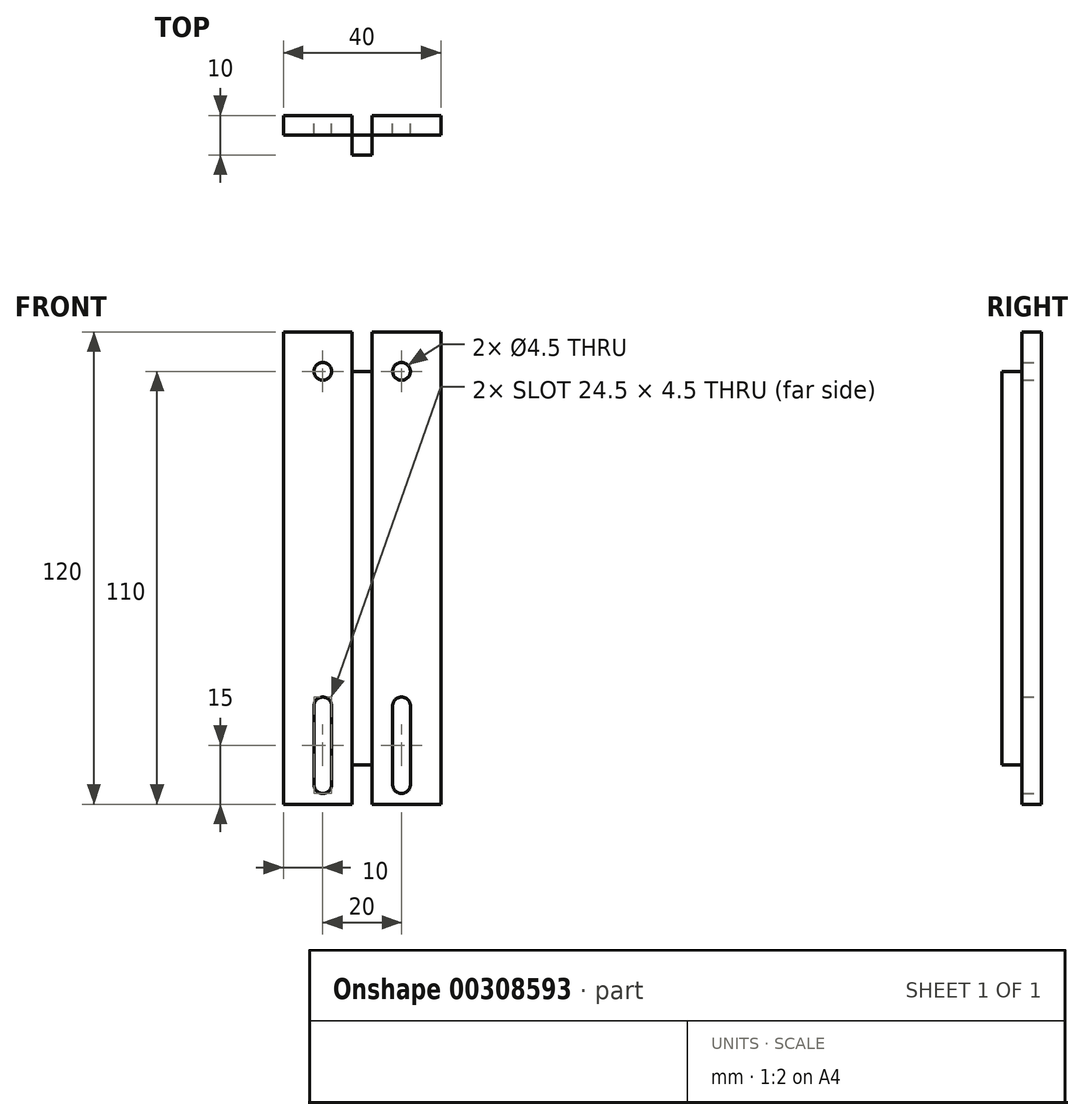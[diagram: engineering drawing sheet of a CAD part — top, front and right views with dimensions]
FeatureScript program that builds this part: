
annotation { "Feature Type Name" : "Feature", "Feature Type Description" : "" }
export const myFeature = defineFeature(function(context is Context, id is Id, definition is map)
    precondition{}
    {
        {
            var Q0;
            Q0=qCreatedBy(makeId("Front.planeOp"),FACE);
            var sketch = newSketch(context, id + "F0", { "sketchPlane" : qUnion([Q0])});
            skLineSegment(sketch, "E0.bottom", {"start": v(-20, 60) * mm, "end": v(20, 60) * mm});
            skLineSegment(sketch, "E0.top", {"start": v(-20, -60) * mm, "end": v(20, -60) * mm});
            skLineSegment(sketch, "E0.left", {"start": v(-20, 60) * mm, "end": v(-20, -60) * mm});
            skLineSegment(sketch, "E0.right", {"start": v(20, 60) * mm, "end": v(20, -60) * mm});
            skPoint(sketch, "E0.middle", {"position": v(0, 0) * mm});
            skPoint(sketch, "E1", {"position": v(-10, 50) * mm});
            skPoint(sketch, "E2", {"position": v(10, 50) * mm});
            skCircle(sketch, "E3", {"center": v(-10, -55) * mm, "radius": 2.25 * mm});
            skCircle(sketch, "E4", {"center": v(10, -55) * mm, "radius": 2.25 * mm});
            skCircle(sketch, "E5", {"center": v(-10, -35) * mm, "radius": 2.25 * mm});
            skCircle(sketch, "E6", {"center": v(10, -35) * mm, "radius": 2.25 * mm});
            skLineSegment(sketch, "E7", {"start": v(-20, -35) * mm, "end": v(20, -35) * mm, "construction": true});
            skLineSegment(sketch, "E8", {"start": v(-20, -55) * mm, "end": v(20, -55) * mm, "construction": true});
            skLineSegment(sketch, "E9", {"start": v(-12.25, -55) * mm, "end": v(-12.25, -35) * mm});
            skLineSegment(sketch, "E10", {"start": v(-7.75, -35) * mm, "end": v(-7.75, -55) * mm});
            skLineSegment(sketch, "E11", {"start": v(7.75, -35) * mm, "end": v(7.75, -55) * mm});
            skLineSegment(sketch, "E12", {"start": v(12.25, -35) * mm, "end": v(12.25, -55) * mm});
            skLineSegment(sketch, "E13.bottom", {"start": v(2.5, 60) * mm, "end": v(-2.5, 60) * mm});
            skLineSegment(sketch, "E13.top", {"start": v(2.5, -60) * mm, "end": v(-2.5, -60) * mm});
            skLineSegment(sketch, "E13.left", {"start": v(2.5, 60) * mm, "end": v(2.5, -60) * mm});
            skLineSegment(sketch, "E13.right", {"start": v(-2.5, 60) * mm, "end": v(-2.5, -60) * mm});
            skSolve(sketch);
        }
        {
            var Q0;
            {var subQ0=sQuery(id+"F0.wireOp",EDGE,"E0.left");Q0=makeQuery(id+"F0.imprint","IMPRINT",FACE,{"disambiguationData":[TD([[makeQuery(id+"F0.imprint","IMPRINT",EDGE,{"derivedFrom":subQ0}),1.0]])]});}
            var Q1;
            Q1=makeQuery(id+"F0.imprint","IMPRINT",FACE,{"disambiguationData":[TD([[makeQuery(id+"F0.imprint","IMPRINT",EDGE,{"derivedFrom":sQuery(id+"F0.wireOp",EDGE,"E13.bottom")}),1.0]])]});
            var Q2;
            {var subQ4=sQuery(id+"F0.wireOp",EDGE,"E0.right");Q2=makeQuery(id+"F0.imprint","IMPRINT",FACE,{"disambiguationData":[TD([[makeQuery(id+"F0.imprint","IMPRINT",EDGE,{"derivedFrom":subQ4}),-1.0]])]});}
            extrude(context, id + "F1", {"entities" : qUnion([Q0, Q1, Q2]), "depth" : 5 * mm});
        }
        {
            var Q0;
            Q0=makeQuery(id+"F1.opExtrude","CAP_FACE",FACE,{"disambiguationData":[OSD([sQuery(id+"F0.wireOp",EDGE,"E0.bottom"),sQuery(id+"F0.wireOp",EDGE,"E0.top"),sQuery(id+"F0.wireOp",EDGE,"E0.left"),sQuery(id+"F0.wireOp",EDGE,"E0.right"),sQuery(id+"F0.wireOp",EDGE,"E3"),sQuery(id+"F0.wireOp",EDGE,"E4"),sQuery(id+"F0.wireOp",EDGE,"E5"),sQuery(id+"F0.wireOp",EDGE,"E6"),sQuery(id+"F0.wireOp",EDGE,"E9"),sQuery(id+"F0.wireOp",EDGE,"E10"),sQuery(id+"F0.wireOp",EDGE,"E11"),sQuery(id+"F0.wireOp",EDGE,"E12"),sQuery(id+"F0.wireOp",EDGE,"E13.bottom"),sQuery(id+"F0.wireOp",EDGE,"E13.top")])],"isStart":false});
            var sketch = newSketch(context, id + "F2", { "sketchPlane" : qUnion([Q0])});
            skLineSegment(sketch, "E14.bottom", {"start": v(2.5, 50) * mm, "end": v(-2.5, 50) * mm});
            skLineSegment(sketch, "E14.top", {"start": v(2.5, -50) * mm, "end": v(-2.5, -50) * mm});
            skLineSegment(sketch, "E14.left", {"start": v(2.5, 50) * mm, "end": v(2.5, -50) * mm});
            skLineSegment(sketch, "E14.right", {"start": v(-2.5, 50) * mm, "end": v(-2.5, -50) * mm});
            skPoint(sketch, "E14.middle", {"position": v(0, 0) * mm});
            skSolve(sketch);
        }
        {
            var Q0;
            Q0=makeQuery(id+"F2.imprint","IMPRINT",FACE,{"disambiguationData":[TD([[makeQuery(id+"F2.imprint","IMPRINT",EDGE,{"derivedFrom":sQuery(id+"F2.wireOp",EDGE,"E14.bottom")}),1.0]])]});
            extrude(context, id + "F3", {"entities" : qUnion([Q0]), "operationType" : NewBodyOperationType.ADD, "depth" : 5 * mm});
        }
        {
            var Q0;
            Q0=sQuery(id+"F0.wireOp",VERTEX,"E2");
            var Q1;
            Q1=sQuery(id+"F0.wireOp",VERTEX,"E1");
            var Q2;
            Q2=makeQuery(id+"F1.opExtrude","SWEPT_BODY",BODY,{"disambiguationData":[OSD([sQuery(id+"F0.wireOp",EDGE,"E0.bottom"),sQuery(id+"F0.wireOp",EDGE,"E0.top"),sQuery(id+"F0.wireOp",EDGE,"E0.left"),sQuery(id+"F0.wireOp",EDGE,"E0.right"),sQuery(id+"F0.wireOp",EDGE,"E3"),sQuery(id+"F0.wireOp",EDGE,"E4"),sQuery(id+"F0.wireOp",EDGE,"E5"),sQuery(id+"F0.wireOp",EDGE,"E6"),sQuery(id+"F0.wireOp",EDGE,"E9"),sQuery(id+"F0.wireOp",EDGE,"E10"),sQuery(id+"F0.wireOp",EDGE,"E11"),sQuery(id+"F0.wireOp",EDGE,"E12"),sQuery(id+"F0.wireOp",EDGE,"E13.bottom"),sQuery(id+"F0.wireOp",EDGE,"E13.top")])]});
            hole(context, id + "F4", {"style" : HoleStyle.SIMPLE, "endStyle" : HoleEndStyle.BLIND, "oppositeDirection" : true, "holeDiameter" : 4.5 * mm, "holeDepth" : 17 * mm, "isTappedThrough" : true, "tappedDepth" : 12 * mm, "tapClearance" : 3, "locations" : qUnion([Q0, Q1]), "scope" : qUnion([Q2])});
        }
    });
